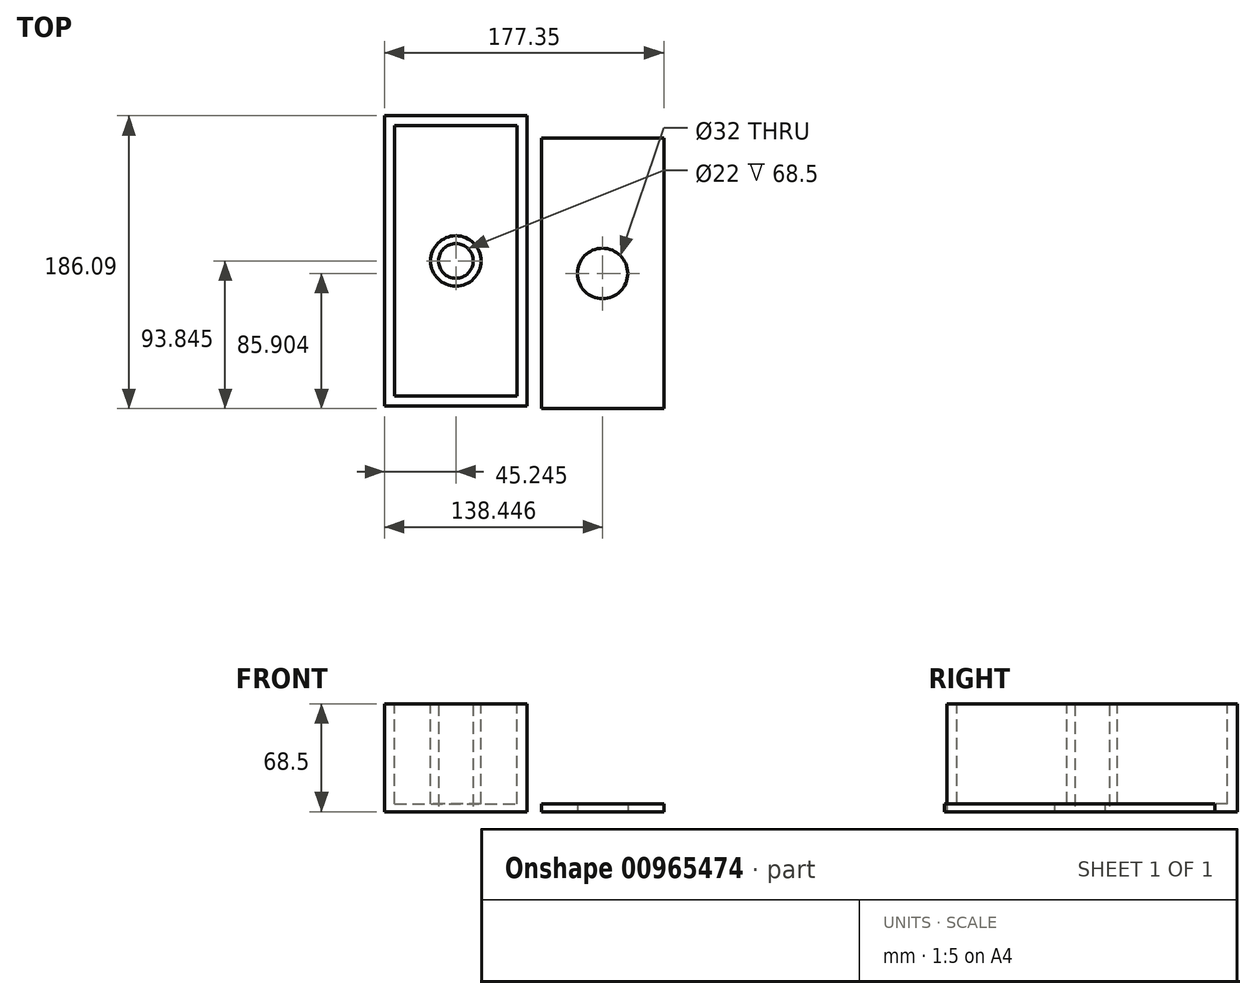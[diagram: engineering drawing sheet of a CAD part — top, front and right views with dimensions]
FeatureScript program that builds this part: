
annotation { "Feature Type Name" : "Feature", "Feature Type Description" : "" }
export const myFeature = defineFeature(function(context is Context, id is Id, definition is map)
    precondition{}
    {
        {
            var Q0;
            Q0=qCreatedBy(makeId("Top.planeOp"),FACE);
            var sketch = newSketch(context, id + "F0", { "sketchPlane" : qUnion([Q0])});
            skLineSegment(sketch, "E0.bottom", {"start": v(-53.28, 149.97) * mm, "end": v(37.22, 149.97) * mm});
            skLineSegment(sketch, "E0.top", {"start": v(-53.28, -34.53) * mm, "end": v(37.22, -34.53) * mm});
            skLineSegment(sketch, "E0.left", {"start": v(-53.28, 149.97) * mm, "end": v(-53.28, -34.53) * mm});
            skLineSegment(sketch, "E0.right", {"start": v(37.22, 149.97) * mm, "end": v(37.22, -34.53) * mm});
            skCircle(sketch, "E1", {"center": v(-8.03, 57.72) * mm, "radius": 11 * mm});
            skPoint(sketch, "E1.centerSnap0", {"position": v(-53.28, 57.72) * mm});
            skPoint(sketch, "E1.centerSnap1", {"position": v(-8.03, 149.97) * mm});
            skSolve(sketch);
        }
        {
            var Q0;
            Q0=makeQuery(id+"F0.imprint","IMPRINT",FACE,{"disambiguationData":[TD([[makeQuery(id+"F0.imprint","IMPRINT",EDGE,{"derivedFrom":sQuery(id+"F0.wireOp",EDGE,"E0.bottom")}),-1.0]])]});
            extrude(context, id + "F1", {"entities" : qUnion([Q0]), "depth" : 68.5 * mm, "offsetDistance" : 25.4 * mm});
        }
        {
            var Q0;
            Q0=makeQuery(id+"F1.opExtrude","CAP_FACE",FACE,{"disambiguationData":[OSD([sQuery(id+"F0.wireOp",EDGE,"E0.bottom"),sQuery(id+"F0.wireOp",EDGE,"E0.top"),sQuery(id+"F0.wireOp",EDGE,"E0.left"),sQuery(id+"F0.wireOp",EDGE,"E0.right"),sQuery(id+"F0.wireOp",EDGE,"E1")])],"isStart":false});
            var sketch = newSketch(context, id + "F2", { "sketchPlane" : qUnion([Q0])});
            skLineSegment(sketch, "E2.0", {"start": v(-46.93, 143.62) * mm, "end": v(30.87, 143.62) * mm});
            skLineSegment(sketch, "E2.1", {"start": v(-46.93, 143.62) * mm, "end": v(-46.93, -28.18) * mm});
            skLineSegment(sketch, "E2.2", {"start": v(-46.93, -28.18) * mm, "end": v(30.87, -28.18) * mm});
            skLineSegment(sketch, "E2.3", {"start": v(30.87, 143.62) * mm, "end": v(30.87, -28.18) * mm});
            skCircle(sketch, "E3", {"center": v(-8.03, 57.72) * mm, "radius": 16 * mm});
            skSolve(sketch);
        }
        {
            var Q0;
            Q0=makeQuery(id+"F2.imprint","IMPRINT",FACE,{"disambiguationData":[TD([[makeQuery(id+"F2.imprint","IMPRINT",EDGE,{"derivedFrom":sQuery(id+"F2.wireOp",EDGE,"E2.0")}),-1.0]])]});
            extrude(context, id + "F3", {"entities" : qUnion([Q0]), "operationType" : NewBodyOperationType.REMOVE, "oppositeDirection" : true, "depth" : 63.5 * mm, "offsetDistance" : 25.4 * mm});
        }
        {
            var Q0;
            Q0=qCreatedBy(makeId("Top.planeOp"),FACE);
            var sketch = newSketch(context, id + "F4", { "sketchPlane" : qUnion([Q0])});
            skLineSegment(sketch, "E4.0", {"start": v(46.27, 135.68) * mm, "end": v(124.07, 135.68) * mm});
            skLineSegment(sketch, "E4.1", {"start": v(46.27, 135.68) * mm, "end": v(46.27, -36.12) * mm});
            skLineSegment(sketch, "E4.2", {"start": v(46.27, -36.12) * mm, "end": v(124.07, -36.12) * mm});
            skLineSegment(sketch, "E4.3", {"start": v(124.07, 135.68) * mm, "end": v(124.07, -36.12) * mm});
            skCircle(sketch, "E5", {"center": v(85.17, 49.78) * mm, "radius": 16 * mm});
            skSolve(sketch);
        }
        {
            var Q0;
            Q0=makeQuery(id+"F4.imprint","IMPRINT",FACE,{"disambiguationData":[TD([[makeQuery(id+"F4.imprint","IMPRINT",EDGE,{"derivedFrom":sQuery(id+"F4.wireOp",EDGE,"E4.0")}),-1.0]])]});
            extrude(context, id + "F5", {"entities" : qUnion([Q0]), "depth" : 5 * mm, "offsetDistance" : 25.4 * mm});
        }
    });
